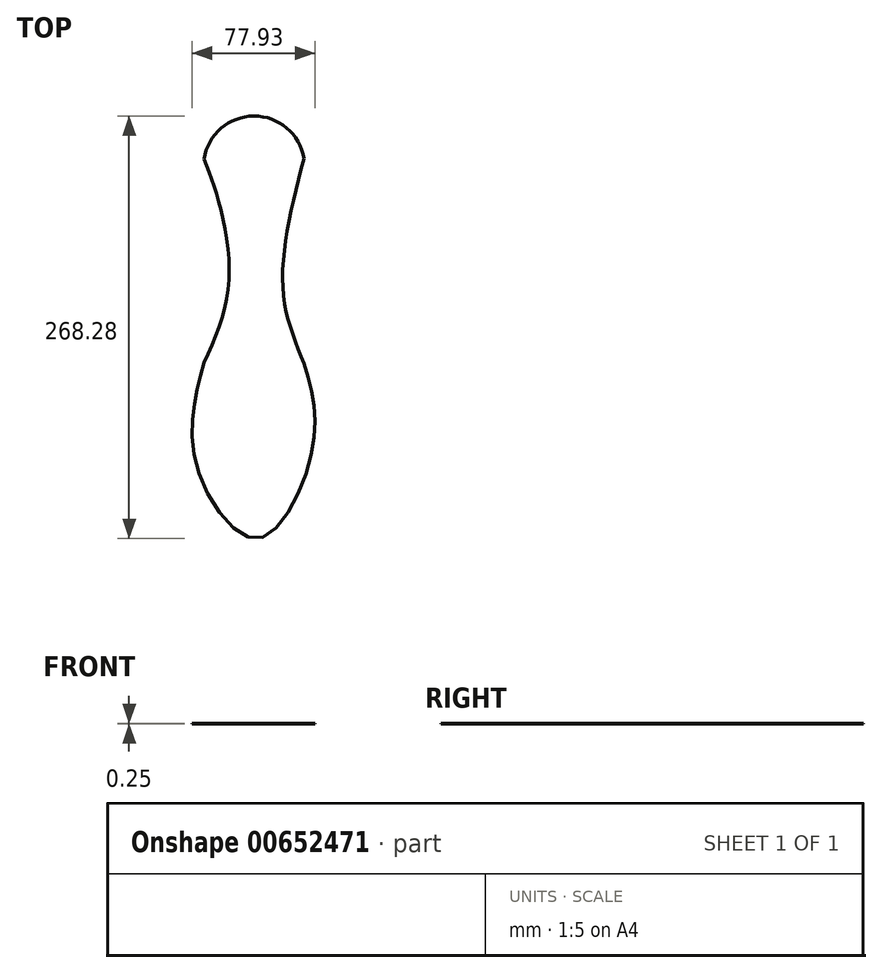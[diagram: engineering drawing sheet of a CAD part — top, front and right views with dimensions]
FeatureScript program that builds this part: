
annotation { "Feature Type Name" : "Feature", "Feature Type Description" : "" }
export const myFeature = defineFeature(function(context is Context, id is Id, definition is map)
    precondition{}
    {
        {
            var Q0;
            Q0=qCreatedBy(makeId("Top.planeOp"),FACE);
            var sketch = newSketch(context, id + "F0", { "sketchPlane" : qUnion([Q0])});
            skArc(sketch, "E0", {"start": v(30.13, 54.4) * mm, "mid": v(-1.7, 81.32) * mm, "end": v(-33.27, 54.12) * mm});
            skFitSpline(sketch, "E1", {"points": [v(30.13, 54.4) * mm, v(16.7, -26.7) * mm, v(30.13, -75.82) * mm], "startDerivative": vector(-39.22, -154.28) * mm, "endDerivative": vector(42.47, -104.17) * mm});
            skFitSpline(sketch, "E2", {"points": [v(-33.27, 54.12) * mm, v(-23.27, 24.42) * mm, v(-17.85, -27.84) * mm, v(-33.27, -75.25) * mm], "startDerivative": vector(36.92, -96.13) * mm, "endDerivative": vector(-57.44, -128.2) * mm});
            skFitSpline(sketch, "E3", {"points": [v(30.13, -75.82) * mm, v(36.77, -105.31) * mm, v(30.13, -149.33) * mm, v(0, -186.95) * mm, v(-35.13, -149.26) * mm, v(-39.7, -103.56) * mm, v(-33.27, -75.25) * mm], "startDerivative": vector(59.9, -198.42) * mm, "endDerivative": vector(53.05, 191.54) * mm});
            skSolve(sketch);
        }
        {
            var Q0;
            Q0=makeQuery(id+"F0.imprint","IMPRINT",FACE,{"disambiguationData":[TD([[makeQuery(id+"F0.imprint","IMPRINT",EDGE,{"derivedFrom":sQuery(id+"F0.wireOp",EDGE,"E0")}),1.0]])]});
            extrude(context, id + "F1", {"entities" : qUnion([Q0]), "depth" : 0.25 * mm, "offsetDistance" : 25.4 * mm});
        }
    });
